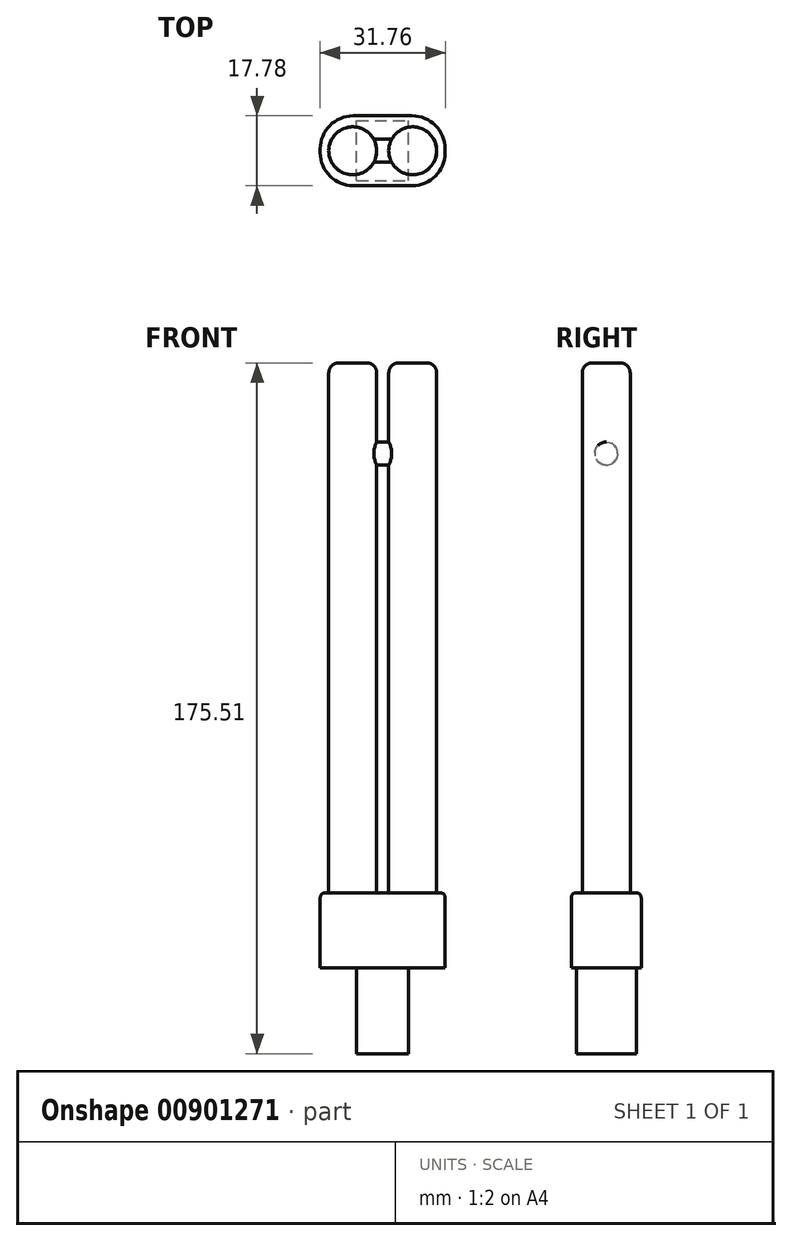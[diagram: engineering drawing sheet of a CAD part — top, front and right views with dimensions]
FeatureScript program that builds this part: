
annotation { "Feature Type Name" : "Feature", "Feature Type Description" : "" }
export const myFeature = defineFeature(function(context is Context, id is Id, definition is map)
    precondition{}
    {
        {
            var Q0;
            Q0=qCreatedBy(makeId("Top.planeOp"),FACE);
            var sketch = newSketch(context, id + "F0", { "sketchPlane" : qUnion([Q0])});
            skCircle(sketch, "E0", {"center": v(7.62, 0) * mm, "radius": 6.1 * mm});
            skCircle(sketch, "E1", {"center": v(-7.62, 0) * mm, "radius": 6.1 * mm});
            skSolve(sketch);
        }
        {
            var Q0;
            Q0=qSketchRegion(id+"F0",true);
            extrude(context, id + "F1", {"entities" : qUnion([Q0]), "depth" : 134.62 * mm, "offsetDistance" : 25.4 * mm});
        }
        {
            var Q0;
            Q0=qCreatedBy(makeId("Right.planeOp"),FACE);
            var sketch = newSketch(context, id + "F2", { "sketchPlane" : qUnion([Q0])});
            skCircle(sketch, "E2", {"center": v(0, 111.6) * mm, "radius": 2.92 * mm});
            skSolve(sketch);
        }
        {
            var Q0;
            Q0=qSketchRegion(id+"F2",true);
            extrude(context, id + "F3", {"entities" : qUnion([Q0]), "operationType" : NewBodyOperationType.ADD, "depth" : 5.08 * mm, "offsetDistance" : 25.4 * mm, "hasSecondDirection" : true, "secondDirectionOppositeDirection" : true, "secondDirectionDepth" : 5.08 * mm});
        }
        {
            var Q0;
            Q0=makeQuery(id+"F1.opExtrude","CAP_FACE",FACE,{"disambiguationData":[OSD([sQuery(id+"F0.wireOp",EDGE,"E1")])],"isStart":false});
            var Q1;
            Q1=makeQuery(id+"F1.opExtrude","CAP_FACE",FACE,{"disambiguationData":[OSD([sQuery(id+"F0.wireOp",EDGE,"E0")])],"isStart":false});
            fillet(context, id + "F4", {"entities" : qUnion([Q0, Q1]), "radius" : 2.54 * mm, "tangentPropagation" : true, "allowEdgeOverflow" : false});
        }
        {
            var Q0;
            Q0=qCreatedBy(makeId("Top.planeOp"),FACE);
            var sketch = newSketch(context, id + "F5", { "sketchPlane" : qUnion([Q0])});
            skLineSegment(sketch, "E3.bottom", {"start": v(-7.5, -8.9) * mm, "end": v(7.5, -8.9) * mm});
            skLineSegment(sketch, "E3.top", {"start": v(-7.5, 8.9) * mm, "end": v(7.5, 8.9) * mm});
            skLineSegment(sketch, "E3.left", {"start": v(-15.88, -0.5) * mm, "end": v(-15.88, 0.5) * mm});
            skLineSegment(sketch, "E3.right", {"start": v(15.88, -0.5) * mm, "end": v(15.88, 0.5) * mm});
            skPoint(sketch, "E3.middle", {"position": v(0, 0) * mm});
            skPoint(sketch, "E4.visualSharp", {"position": v(-15.88, -8.9) * mm});
            skArc(sketch, "E4.filletArc", {"start": v(-15.88, -0.5) * mm, "mid": v(-13.42, -6.43) * mm, "end": v(-7.5, -8.9) * mm});
            skPoint(sketch, "E5.visualSharp", {"position": v(-15.88, 8.9) * mm});
            skArc(sketch, "E5.filletArc", {"start": v(-7.5, 8.9) * mm, "mid": v(-13.42, 6.43) * mm, "end": v(-15.88, 0.5) * mm});
            skPoint(sketch, "E6.visualSharp", {"position": v(15.88, -8.9) * mm});
            skArc(sketch, "E6.filletArc", {"start": v(7.5, -8.9) * mm, "mid": v(13.42, -6.43) * mm, "end": v(15.88, -0.5) * mm});
            skPoint(sketch, "E7.visualSharp", {"position": v(15.88, 8.9) * mm});
            skArc(sketch, "E7.filletArc", {"start": v(15.88, 0.5) * mm, "mid": v(13.42, 6.43) * mm, "end": v(7.5, 8.9) * mm});
            skSolve(sketch);
        }
        {
            var Q0;
            Q0=qSketchRegion(id+"F5",true);
            extrude(context, id + "F6", {"entities" : qUnion([Q0]), "operationType" : NewBodyOperationType.ADD, "oppositeDirection" : true, "depth" : 19.05 * mm, "offsetDistance" : 25.4 * mm});
        }
        {
            var Q0;
            Q0=makeQuery(id+"F6.opExtrude","CAP_EDGE",EDGE,{"disambiguationData":[OSD([sQuery(id+"F5.wireOp",EDGE,"E3.bottom")])],"isStart":true});
            fillet(context, id + "F7", {"entities" : qUnion([Q0]), "radius" : 1.27 * mm, "tangentPropagation" : true, "allowEdgeOverflow" : false});
        }
        {
            var Q0;
            Q0=makeQuery(id+"F6.opExtrude","CAP_FACE",FACE,{"disambiguationData":[OSD([sQuery(id+"F5.wireOp",EDGE,"E3.bottom"),sQuery(id+"F5.wireOp",EDGE,"E3.top"),sQuery(id+"F5.wireOp",EDGE,"E3.left"),sQuery(id+"F5.wireOp",EDGE,"E3.right"),sQuery(id+"F5.wireOp",EDGE,"E4.filletArc"),sQuery(id+"F5.wireOp",EDGE,"E5.filletArc"),sQuery(id+"F5.wireOp",EDGE,"E6.filletArc"),sQuery(id+"F5.wireOp",EDGE,"E7.filletArc")])],"isStart":false});
            var sketch = newSketch(context, id + "F8", { "sketchPlane" : qUnion([Q0])});
            skLineSegment(sketch, "E8.bottom", {"start": v(-6.6, 7.62) * mm, "end": v(6.6, 7.62) * mm});
            skLineSegment(sketch, "E8.top", {"start": v(-6.6, -7.62) * mm, "end": v(6.6, -7.62) * mm});
            skLineSegment(sketch, "E8.left", {"start": v(-6.6, 7.62) * mm, "end": v(-6.6, -7.62) * mm});
            skLineSegment(sketch, "E8.right", {"start": v(6.6, 7.62) * mm, "end": v(6.6, -7.62) * mm});
            skPoint(sketch, "E8.middle", {"position": v(0, 0) * mm});
            skSolve(sketch);
        }
        {
            var Q0;
            Q0 = qSketchRegion(id + "F8", true);
            extrude(context, id + "F9", {"entities" : qUnion([Q0]), "operationType" : NewBodyOperationType.ADD, "depth" : 21.84 * mm, "offsetDistance" : 25.4 * mm});
        }
    });
